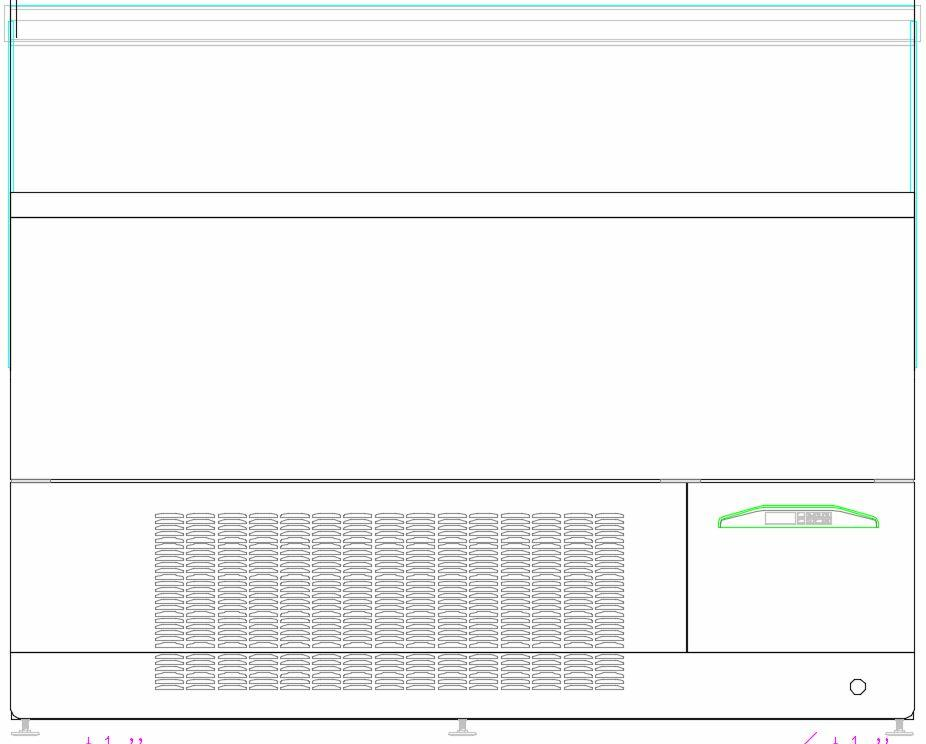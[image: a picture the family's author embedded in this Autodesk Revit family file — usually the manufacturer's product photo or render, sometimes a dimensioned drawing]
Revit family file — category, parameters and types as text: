
# Revit family: QF_OSCARTEK_VENTURA_G1610_cat
name_source: partatom
category: Specialty Equipment
units: mm (PartAtom-declared; Revit-internal decimal feet)

## family parameters
Always vertical = Yes
Cut with Voids When Loaded = No
Enable Cutting in Views = No
Maintain Annotation Orientation = No
Part Type = Normal
Room Calculation Point = No
Round Connector Dimension = Use Diameter
Shared = No
Work Plane-Based = No

## types (1)
- QF_OSCARTEK_VENTURA_G1610_cat
    Apparent Power = 1747 VA
    BTUH = 9696.0 Btu/h
    Conn Conduit = Yes
    Cycle = 50 Hz
    Default Elevation = 0"
    Depth = 44 15/16"
    Description = GELATO CASE
    Elec Conn Connection Height = 0"
    Elec Conn RI Height = 0"
    FL Amps = 8 A
    Foodservice Equipment Identifier = Yes
    Height = 51 3/16"
    Identify Quantity as Lot = Yes
    Indirect Waste Connection Height = 0"
    Indirect Waste Flow = 0 GPM
    Indirect Waste Size = 1"
    Length = 63 3/8"
    Manufacturer = OSCARTEK
    Max Overcurrent Protection = 0 A
    Min Ckt Ampacity = 0 A
    Model = VENTURA G1610
    Number of Poles = 1
    Phase = 1
    Refrigerant Type = R404A
    Refrigerant Volume = 0.00 kip
    Volts = 208 V
    Waste Water Discharge Temperature = 0 °F
    Watts = 3030 W
    Weight in Pounds = 687

## geometry (parser evidence)
native form markers: Blend x8, Sweep x9
no freeform markers — native parametric forms only
